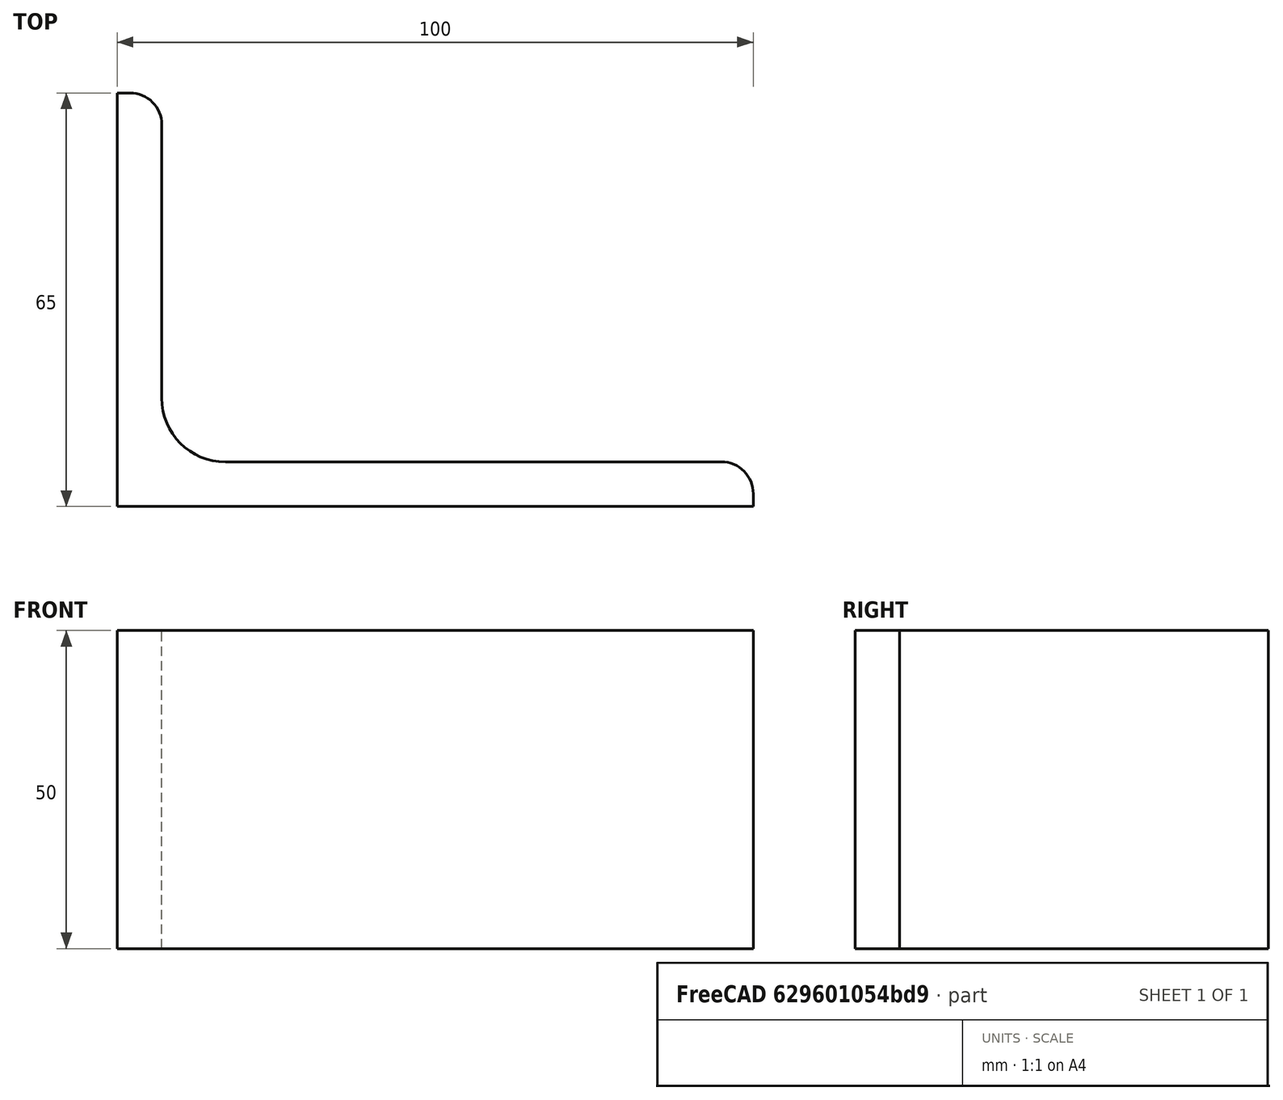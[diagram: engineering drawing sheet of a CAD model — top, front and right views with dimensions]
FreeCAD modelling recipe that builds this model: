
FCSTD DOCUMENT  (FreeCAD 0.15R4671 (Git))
Label: Angle Bar 100x65x7 EN10056 S235JR
License: All rights reserved
LicenseURL: http://en.wikipedia.org/wiki/All_rights_reserved
objects: Sketcher::SketchObject×1, Part::Extrusion×1
note: 2 computed .brp shape members not serialized (recipe doc carries the construction recipe); baked Part::Feature solids carry a one-line shape summary decoded from their .brp

FEATURE [Sketcher::SketchObject] Sketch
  sketch-geometry (9):
    g0: LineSegment StartX=0 StartY=0 StartZ=0 EndX=100 EndY=0 EndZ=0
    g1: LineSegment StartX=100 StartY=0 StartZ=0 EndX=100 EndY=2 EndZ=0
    g2: LineSegment StartX=95 StartY=7 StartZ=0 EndX=17 EndY=7 EndZ=0
    g3: LineSegment StartX=0 StartY=0 StartZ=0 EndX=0 EndY=65 EndZ=0
    g4: LineSegment StartX=0 StartY=65 StartZ=0 EndX=2 EndY=65 EndZ=0
    g5: LineSegment StartX=7 StartY=60 StartZ=0 EndX=7 EndY=17 EndZ=0
    g6: ArcOfCircle CenterX=17 CenterY=17 CenterZ=0 NormalX=0 NormalY=0 NormalZ=1 Radius=10 StartAngle=3.14159 EndAngle=4.71239
    g7: ArcOfCircle CenterX=2 CenterY=60 CenterZ=0 NormalX=0 NormalY=0 NormalZ=1 Radius=5 StartAngle=0 EndAngle=1.5708
    g8: ArcOfCircle CenterX=95 CenterY=2 CenterZ=0 NormalX=0 NormalY=0 NormalZ=1 Radius=5 StartAngle=0 EndAngle=1.5708
  constraints (23):
    c: Coincident(g0,g-1)
    c: Horizontal(g0)
    c: Coincident(g1,g0)
    c: Vertical(g1)
    c: Horizontal(g2)
    c: Coincident(g3,g-1)
    c: Vertical(g3)
    c: Coincident(g4,g3)
    c: Horizontal(g4)
    c: Vertical(g5)
    c: Tangent(g5,g6) = -1.5708
    c: Tangent(g2,g6) = 1.5708
    c: Tangent(g4,g7) = 1.5708
    c: Tangent(g5,g7) = 1.5708
    c: Tangent(g2,g8) = -1.5708
    c: Tangent(g1,g8) = -1.5708
    c: DistanceX(g0) = 100
    c: DistanceY(g3) = 65
    c: DistanceY(g0,g2) = 7
    c: DistanceX(g3,g5) = 7
    c: Radius(g6) = 10
    c: Radius(g8) = 5
    c: Radius(g7) = 5
FEATURE [Part::Extrusion] Extrude  label="Angle Bar 100x65x7 EN10056 S235JR"
  Base = -> Sketch
  Dir = (0,0,50)
  Solid = true
